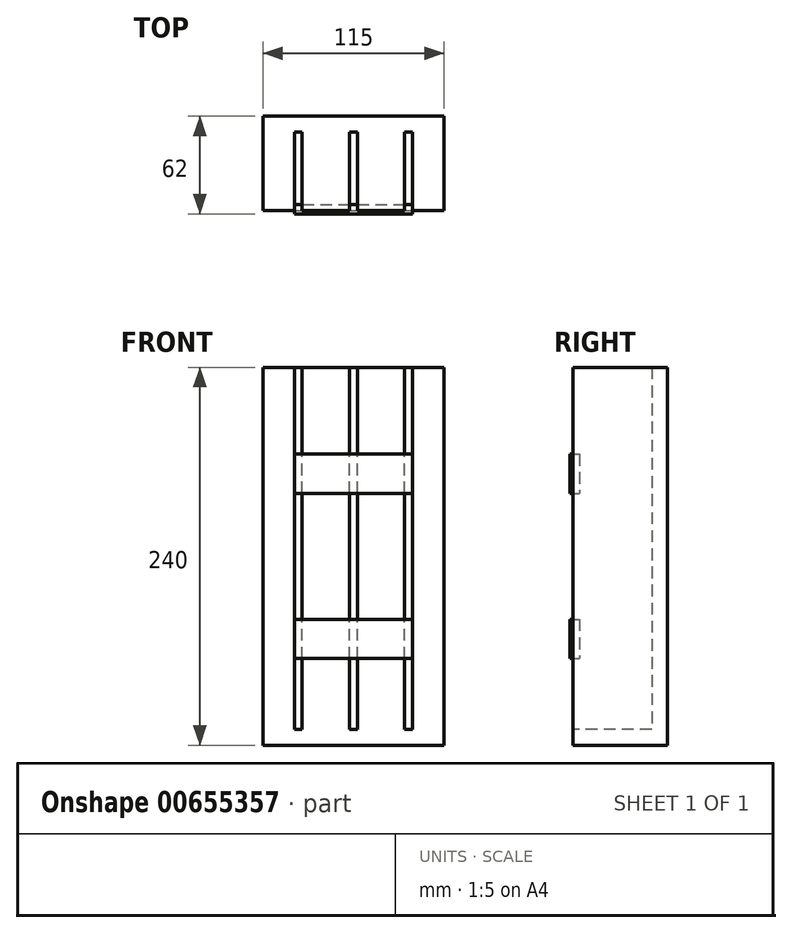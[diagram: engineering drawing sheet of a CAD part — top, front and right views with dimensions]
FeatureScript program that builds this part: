
annotation { "Feature Type Name" : "Feature", "Feature Type Description" : "" }
export const myFeature = defineFeature(function(context is Context, id is Id, definition is map)
    precondition{}
    {
        {
            var Q0;
            Q0=qCreatedBy(makeId("Front.planeOp"),FACE);
            var sketch = newSketch(context, id + "F0", { "sketchPlane" : qUnion([Q0])});
            skLineSegment(sketch, "E0.bottom", {"start": v(-57.5, 103.2) * mm, "end": v(57.5, 103.2) * mm});
            skLineSegment(sketch, "E0.top", {"start": v(-57.5, -136.8) * mm, "end": v(57.5, -136.8) * mm});
            skLineSegment(sketch, "E0.left", {"start": v(-57.5, 103.2) * mm, "end": v(-57.5, -136.8) * mm});
            skLineSegment(sketch, "E0.right", {"start": v(57.5, 103.2) * mm, "end": v(57.5, -136.8) * mm});
            skPoint(sketch, "E0.middle", {"position": v(0, -16.8) * mm});
            skLineSegment(sketch, "E1.bottom", {"start": v(-57.5, 103.2) * mm, "end": v(-37.5, 103.2) * mm});
            skLineSegment(sketch, "E1.top", {"start": v(-57.5, -136.8) * mm, "end": v(-37.5, -136.8) * mm});
            skLineSegment(sketch, "E1.right", {"start": v(-37.5, 103.2) * mm, "end": v(-37.5, -136.8) * mm});
            skLineSegment(sketch, "E2.bottom", {"start": v(57.5, 103.2) * mm, "end": v(37.5, 103.2) * mm});
            skLineSegment(sketch, "E2.top", {"start": v(57.5, -136.8) * mm, "end": v(37.5, -136.8) * mm});
            skLineSegment(sketch, "E2.right", {"start": v(37.5, 103.2) * mm, "end": v(37.5, -136.8) * mm});
            skLineSegment(sketch, "E3.bottom", {"start": v(-32.5, 103.2) * mm, "end": v(-2.5, 103.2) * mm});
            skLineSegment(sketch, "E3.top", {"start": v(-32.5, -126.8) * mm, "end": v(-2.5, -126.8) * mm});
            skLineSegment(sketch, "E3.left", {"start": v(-32.5, 103.2) * mm, "end": v(-32.5, -126.8) * mm});
            skLineSegment(sketch, "E3.right", {"start": v(-2.5, 103.2) * mm, "end": v(-2.5, -126.8) * mm});
            skLineSegment(sketch, "E4.bottom", {"start": v(2.5, 103.2) * mm, "end": v(32.5, 103.2) * mm});
            skLineSegment(sketch, "E4.top", {"start": v(2.5, -126.8) * mm, "end": v(32.5, -126.8) * mm});
            skLineSegment(sketch, "E4.left", {"start": v(2.5, 103.2) * mm, "end": v(2.5, -126.8) * mm});
            skLineSegment(sketch, "E4.right", {"start": v(32.5, 103.2) * mm, "end": v(32.5, -126.8) * mm});
            skLineSegment(sketch, "E5.top", {"start": v(-57.5, -126.8) * mm, "end": v(57.5, -126.8) * mm});
            skLineSegment(sketch, "E5.left", {"start": v(-57.5, -136.8) * mm, "end": v(-57.5, -126.8) * mm});
            skLineSegment(sketch, "E5.right", {"start": v(57.5, -136.8) * mm, "end": v(57.5, -126.8) * mm});
            skLineSegment(sketch, "E6.bottom", {"start": v(-57.5, 48.2) * mm, "end": v(57.5, 48.2) * mm});
            skLineSegment(sketch, "E6.top", {"start": v(-57.5, 23.2) * mm, "end": v(57.5, 23.2) * mm});
            skLineSegment(sketch, "E6.left", {"start": v(-57.5, 48.2) * mm, "end": v(-57.5, 23.2) * mm});
            skLineSegment(sketch, "E6.right", {"start": v(57.5, 48.2) * mm, "end": v(57.5, 23.2) * mm});
            skLineSegment(sketch, "E7.bottom", {"start": v(-57.5, -56.8) * mm, "end": v(57.5, -56.8) * mm});
            skLineSegment(sketch, "E7.top", {"start": v(-57.5, -81.8) * mm, "end": v(57.5, -81.8) * mm});
            skLineSegment(sketch, "E7.left", {"start": v(-57.5, -56.8) * mm, "end": v(-57.5, -81.8) * mm});
            skLineSegment(sketch, "E7.right", {"start": v(57.5, -56.8) * mm, "end": v(57.5, -81.8) * mm});
            skSolve(sketch);
        }
        {
            var Q0;
            Q0 = qSketchRegion(id + "F0", true);
            var Q1;
            {var subQ0=sQuery(id+"F0.wireOp",EDGE,"E7.top");var subQ1=sQuery(id+"F0.wireOp",EDGE,"E1.right");var subQ2=makeQuery(id+"F0.imprint","INTERSECT",VERTEX,{"derivedFrom":[subQ1,subQ0]});Q1=makeQuery(id+"F0.imprint","IMPRINT",FACE,{"disambiguationData":[TD([[makeQuery(id+"F0.imprint","IMPRINT",EDGE,{"disambiguationData":[TD([[subQ2,-1.0]])],"derivedFrom":subQ1}),1.0]])]});}
            var Q2;
            {var subQ0=sQuery(id+"F0.wireOp",EDGE,"E5.top");var subQ1=sQuery(id+"F0.wireOp",EDGE,"E3.left");var subQ2=makeQuery(id+"F0.imprint","INTERSECT",VERTEX,{"derivedFrom":[subQ1,subQ0]});Q2=makeQuery(id+"F0.imprint","IMPRINT",FACE,{"disambiguationData":[TD([[makeQuery(id+"F0.imprint","IMPRINT",EDGE,{"disambiguationData":[TD([[subQ2,1.0]])],"derivedFrom":subQ1}),1.0]])]});}
            var Q3;
            {var subQ0=sQuery(id+"F0.wireOp",EDGE,"E6.top");var subQ1=sQuery(id+"F0.wireOp",EDGE,"E3.left");var subQ2=makeQuery(id+"F0.imprint","INTERSECT",VERTEX,{"derivedFrom":[subQ1,subQ0]});Q3=makeQuery(id+"F0.imprint","IMPRINT",FACE,{"disambiguationData":[TD([[makeQuery(id+"F0.imprint","IMPRINT",EDGE,{"disambiguationData":[TD([[subQ2,-1.0]])],"derivedFrom":subQ1}),1.0]])]});}
            var Q4;
            {var subQ0=sQuery(id+"F0.wireOp",EDGE,"E6.bottom");var subQ1=sQuery(id+"F0.wireOp",EDGE,"E3.left");var subQ2=makeQuery(id+"F0.imprint","INTERSECT",VERTEX,{"derivedFrom":[subQ1,subQ0]});Q4=makeQuery(id+"F0.imprint","IMPRINT",FACE,{"disambiguationData":[TD([[makeQuery(id+"F0.imprint","IMPRINT",EDGE,{"disambiguationData":[TD([[subQ2,-1.0]])],"derivedFrom":subQ1}),1.0]])]});}
            var Q5;
            {var subQ0=sQuery(id+"F0.wireOp",EDGE,"E7.bottom");var subQ1=sQuery(id+"F0.wireOp",EDGE,"E3.left");var subQ2=makeQuery(id+"F0.imprint","INTERSECT",VERTEX,{"derivedFrom":[subQ1,subQ0]});Q5=makeQuery(id+"F0.imprint","IMPRINT",FACE,{"disambiguationData":[TD([[makeQuery(id+"F0.imprint","IMPRINT",EDGE,{"disambiguationData":[TD([[subQ2,-1.0]])],"derivedFrom":subQ1}),1.0]])]});}
            var Q6;
            {var subQ0=sQuery(id+"F0.wireOp",EDGE,"E7.bottom");var subQ1=sQuery(id+"F0.wireOp",EDGE,"E1.right");var subQ2=makeQuery(id+"F0.imprint","INTERSECT",VERTEX,{"derivedFrom":[subQ1,subQ0]});Q6=makeQuery(id+"F0.imprint","IMPRINT",FACE,{"disambiguationData":[TD([[makeQuery(id+"F0.imprint","IMPRINT",EDGE,{"disambiguationData":[TD([[subQ2,-1.0]])],"derivedFrom":subQ1}),1.0]])]});}
            var Q7;
            {var subQ0=sQuery(id+"F0.wireOp",EDGE,"E6.top");var subQ1=sQuery(id+"F0.wireOp",EDGE,"E1.right");var subQ2=makeQuery(id+"F0.imprint","INTERSECT",VERTEX,{"derivedFrom":[subQ1,subQ0]});Q7=makeQuery(id+"F0.imprint","IMPRINT",FACE,{"disambiguationData":[TD([[makeQuery(id+"F0.imprint","IMPRINT",EDGE,{"disambiguationData":[TD([[subQ2,-1.0]])],"derivedFrom":subQ1}),1.0]])]});}
            var Q8;
            {var subQ0=sQuery(id+"F0.wireOp",EDGE,"E6.bottom");var subQ1=sQuery(id+"F0.wireOp",EDGE,"E1.right");var subQ2=makeQuery(id+"F0.imprint","INTERSECT",VERTEX,{"derivedFrom":[subQ1,subQ0]});Q8=makeQuery(id+"F0.imprint","IMPRINT",FACE,{"disambiguationData":[TD([[makeQuery(id+"F0.imprint","IMPRINT",EDGE,{"disambiguationData":[TD([[subQ2,-1.0]])],"derivedFrom":subQ1}),1.0]])]});}
            var Q9;
            {var subQ0=sQuery(id+"F0.wireOp",EDGE,"E6.bottom");var subQ1=sQuery(id+"F0.wireOp",EDGE,"E3.right");var subQ2=makeQuery(id+"F0.imprint","INTERSECT",VERTEX,{"derivedFrom":[subQ1,subQ0]});Q9=makeQuery(id+"F0.imprint","IMPRINT",FACE,{"disambiguationData":[TD([[makeQuery(id+"F0.imprint","IMPRINT",EDGE,{"disambiguationData":[TD([[subQ2,-1.0]])],"derivedFrom":subQ1}),1.0]])]});}
            var Q10;
            {var subQ0=sQuery(id+"F0.wireOp",EDGE,"E6.bottom");var subQ1=sQuery(id+"F0.wireOp",EDGE,"E4.left");var subQ2=makeQuery(id+"F0.imprint","INTERSECT",VERTEX,{"derivedFrom":[subQ1,subQ0]});Q10=makeQuery(id+"F0.imprint","IMPRINT",FACE,{"disambiguationData":[TD([[makeQuery(id+"F0.imprint","IMPRINT",EDGE,{"disambiguationData":[TD([[subQ2,-1.0]])],"derivedFrom":subQ1}),1.0]])]});}
            var Q11;
            {var subQ0=sQuery(id+"F0.wireOp",EDGE,"E6.bottom");var subQ1=sQuery(id+"F0.wireOp",EDGE,"E2.right");var subQ2=makeQuery(id+"F0.imprint","INTERSECT",VERTEX,{"derivedFrom":[subQ1,subQ0]});Q11=makeQuery(id+"F0.imprint","IMPRINT",FACE,{"disambiguationData":[TD([[makeQuery(id+"F0.imprint","IMPRINT",EDGE,{"disambiguationData":[TD([[subQ2,-1.0]])],"derivedFrom":subQ1}),-1.0]])]});}
            var Q12;
            {var subQ0=sQuery(id+"F0.wireOp",EDGE,"E6.top");var subQ1=sQuery(id+"F0.wireOp",EDGE,"E2.right");var subQ2=makeQuery(id+"F0.imprint","INTERSECT",VERTEX,{"derivedFrom":[subQ1,subQ0]});Q12=makeQuery(id+"F0.imprint","IMPRINT",FACE,{"disambiguationData":[TD([[makeQuery(id+"F0.imprint","IMPRINT",EDGE,{"disambiguationData":[TD([[subQ2,-1.0]])],"derivedFrom":subQ1}),-1.0]])]});}
            var Q13;
            {var subQ0=sQuery(id+"F0.wireOp",EDGE,"E6.top");var subQ1=sQuery(id+"F0.wireOp",EDGE,"E4.left");var subQ2=makeQuery(id+"F0.imprint","INTERSECT",VERTEX,{"derivedFrom":[subQ1,subQ0]});Q13=makeQuery(id+"F0.imprint","IMPRINT",FACE,{"disambiguationData":[TD([[makeQuery(id+"F0.imprint","IMPRINT",EDGE,{"disambiguationData":[TD([[subQ2,-1.0]])],"derivedFrom":subQ1}),1.0]])]});}
            var Q14;
            {var subQ0=sQuery(id+"F0.wireOp",EDGE,"E6.top");var subQ1=sQuery(id+"F0.wireOp",EDGE,"E3.right");var subQ2=makeQuery(id+"F0.imprint","INTERSECT",VERTEX,{"derivedFrom":[subQ1,subQ0]});Q14=makeQuery(id+"F0.imprint","IMPRINT",FACE,{"disambiguationData":[TD([[makeQuery(id+"F0.imprint","IMPRINT",EDGE,{"disambiguationData":[TD([[subQ2,-1.0]])],"derivedFrom":subQ1}),1.0]])]});}
            var Q15;
            {var subQ0=sQuery(id+"F0.wireOp",EDGE,"E6.top");var subQ1=sQuery(id+"F0.wireOp",EDGE,"E3.right");var subQ2=makeQuery(id+"F0.imprint","INTERSECT",VERTEX,{"derivedFrom":[subQ1,subQ0]});Q15=makeQuery(id+"F0.imprint","IMPRINT",FACE,{"disambiguationData":[TD([[makeQuery(id+"F0.imprint","IMPRINT",EDGE,{"disambiguationData":[TD([[subQ2,-1.0]])],"derivedFrom":subQ1}),1.0]])]});}
            var Q16;
            {var subQ0=sQuery(id+"F0.wireOp",EDGE,"E6.top");var subQ1=sQuery(id+"F0.wireOp",EDGE,"E4.left");var subQ2=makeQuery(id+"F0.imprint","INTERSECT",VERTEX,{"derivedFrom":[subQ1,subQ0]});Q16=makeQuery(id+"F0.imprint","IMPRINT",FACE,{"disambiguationData":[TD([[makeQuery(id+"F0.imprint","IMPRINT",EDGE,{"disambiguationData":[TD([[subQ2,-1.0]])],"derivedFrom":subQ1}),1.0]])]});}
            var Q17;
            {var subQ0=sQuery(id+"F0.wireOp",EDGE,"E7.bottom");var subQ1=sQuery(id+"F0.wireOp",EDGE,"E3.right");var subQ2=makeQuery(id+"F0.imprint","INTERSECT",VERTEX,{"derivedFrom":[subQ1,subQ0]});Q17=makeQuery(id+"F0.imprint","IMPRINT",FACE,{"disambiguationData":[TD([[makeQuery(id+"F0.imprint","IMPRINT",EDGE,{"disambiguationData":[TD([[subQ2,-1.0]])],"derivedFrom":subQ1}),1.0]])]});}
            var Q18;
            {var subQ0=sQuery(id+"F0.wireOp",EDGE,"E5.top");var subQ1=sQuery(id+"F0.wireOp",EDGE,"E3.right");var subQ2=makeQuery(id+"F0.imprint","INTERSECT",VERTEX,{"derivedFrom":[subQ1,subQ0]});Q18=makeQuery(id+"F0.imprint","IMPRINT",FACE,{"disambiguationData":[TD([[makeQuery(id+"F0.imprint","IMPRINT",EDGE,{"disambiguationData":[TD([[subQ2,1.0]])],"derivedFrom":subQ1}),1.0]])]});}
            var Q19;
            {var subQ0=sQuery(id+"F0.wireOp",EDGE,"E5.top");var subQ1=sQuery(id+"F0.wireOp",EDGE,"E4.left");var subQ2=makeQuery(id+"F0.imprint","INTERSECT",VERTEX,{"derivedFrom":[subQ1,subQ0]});Q19=makeQuery(id+"F0.imprint","IMPRINT",FACE,{"disambiguationData":[TD([[makeQuery(id+"F0.imprint","IMPRINT",EDGE,{"disambiguationData":[TD([[subQ2,1.0]])],"derivedFrom":subQ1}),1.0]])]});}
            var Q20;
            {var subQ0=sQuery(id+"F0.wireOp",EDGE,"E7.top");var subQ1=sQuery(id+"F0.wireOp",EDGE,"E2.right");var subQ2=makeQuery(id+"F0.imprint","INTERSECT",VERTEX,{"derivedFrom":[subQ1,subQ0]});Q20=makeQuery(id+"F0.imprint","IMPRINT",FACE,{"disambiguationData":[TD([[makeQuery(id+"F0.imprint","IMPRINT",EDGE,{"disambiguationData":[TD([[subQ2,-1.0]])],"derivedFrom":subQ1}),-1.0]])]});}
            var Q21;
            {var subQ0=sQuery(id+"F0.wireOp",EDGE,"E7.bottom");var subQ1=sQuery(id+"F0.wireOp",EDGE,"E2.right");var subQ2=makeQuery(id+"F0.imprint","INTERSECT",VERTEX,{"derivedFrom":[subQ1,subQ0]});Q21=makeQuery(id+"F0.imprint","IMPRINT",FACE,{"disambiguationData":[TD([[makeQuery(id+"F0.imprint","IMPRINT",EDGE,{"disambiguationData":[TD([[subQ2,-1.0]])],"derivedFrom":subQ1}),-1.0]])]});}
            var Q22;
            {var subQ0=sQuery(id+"F0.wireOp",EDGE,"E7.bottom");var subQ1=sQuery(id+"F0.wireOp",EDGE,"E4.left");var subQ2=makeQuery(id+"F0.imprint","INTERSECT",VERTEX,{"derivedFrom":[subQ1,subQ0]});Q22=makeQuery(id+"F0.imprint","IMPRINT",FACE,{"disambiguationData":[TD([[makeQuery(id+"F0.imprint","IMPRINT",EDGE,{"disambiguationData":[TD([[subQ2,-1.0]])],"derivedFrom":subQ1}),1.0]])]});}
            extrude(context, id + "F1", {"entities" : qUnion([Q0, Q1, Q2, Q3, Q4, Q5, Q6, Q7, Q8, Q9, Q10, Q11, Q12, Q13, Q14, Q15, Q16, Q17, Q18, Q19, Q20, Q21, Q22]), "oppositeDirection" : true, "depth" : 60 * mm, "offsetDistance" : 25 * mm});
        }
        {
            var Q0;
            {var subQ0=sQuery(id+"F0.wireOp",EDGE,"E1.right");var subQ5=sQuery(id+"F0.wireOp",EDGE,"E6.bottom");var subQ6=makeQuery(id+"F0.imprint","INTERSECT",VERTEX,{"derivedFrom":[subQ0,subQ5]});Q0=makeQuery(id+"F0.imprint","IMPRINT",FACE,{"disambiguationData":[TD([[makeQuery(id+"F0.imprint","IMPRINT",EDGE,{"disambiguationData":[TD([[subQ6,-1.0]])],"derivedFrom":subQ5}),1.0]])]});}
            var Q1;
            {var subQ0=sQuery(id+"F0.wireOp",EDGE,"E6.bottom");var subQ1=sQuery(id+"F0.wireOp",EDGE,"E1.right");var subQ2=makeQuery(id+"F0.imprint","INTERSECT",VERTEX,{"derivedFrom":[subQ1,subQ0]});Q1=makeQuery(id+"F0.imprint","IMPRINT",FACE,{"disambiguationData":[TD([[makeQuery(id+"F0.imprint","IMPRINT",EDGE,{"disambiguationData":[TD([[subQ2,-1.0]])],"derivedFrom":subQ1}),1.0]])]});}
            var Q2;
            {var subQ0=sQuery(id+"F0.wireOp",EDGE,"E6.top");var subQ1=sQuery(id+"F0.wireOp",EDGE,"E1.right");var subQ2=makeQuery(id+"F0.imprint","INTERSECT",VERTEX,{"derivedFrom":[subQ1,subQ0]});Q2=makeQuery(id+"F0.imprint","IMPRINT",FACE,{"disambiguationData":[TD([[makeQuery(id+"F0.imprint","IMPRINT",EDGE,{"disambiguationData":[TD([[subQ2,-1.0]])],"derivedFrom":subQ1}),1.0]])]});}
            var Q3;
            {var subQ0=sQuery(id+"F0.wireOp",EDGE,"E7.bottom");var subQ1=sQuery(id+"F0.wireOp",EDGE,"E1.right");var subQ2=makeQuery(id+"F0.imprint","INTERSECT",VERTEX,{"derivedFrom":[subQ1,subQ0]});Q3=makeQuery(id+"F0.imprint","IMPRINT",FACE,{"disambiguationData":[TD([[makeQuery(id+"F0.imprint","IMPRINT",EDGE,{"disambiguationData":[TD([[subQ2,-1.0]])],"derivedFrom":subQ1}),1.0]])]});}
            var Q4;
            {var subQ0=sQuery(id+"F0.wireOp",EDGE,"E7.top");var subQ1=sQuery(id+"F0.wireOp",EDGE,"E1.right");var subQ2=makeQuery(id+"F0.imprint","INTERSECT",VERTEX,{"derivedFrom":[subQ1,subQ0]});Q4=makeQuery(id+"F0.imprint","IMPRINT",FACE,{"disambiguationData":[TD([[makeQuery(id+"F0.imprint","IMPRINT",EDGE,{"disambiguationData":[TD([[subQ2,-1.0]])],"derivedFrom":subQ1}),1.0]])]});}
            var Q5;
            {var subQ0=sQuery(id+"F0.wireOp",EDGE,"E5.top");var subQ1=sQuery(id+"F0.wireOp",EDGE,"E3.right");var subQ2=makeQuery(id+"F0.imprint","INTERSECT",VERTEX,{"derivedFrom":[subQ1,subQ0]});Q5=makeQuery(id+"F0.imprint","IMPRINT",FACE,{"disambiguationData":[TD([[makeQuery(id+"F0.imprint","IMPRINT",EDGE,{"disambiguationData":[TD([[subQ2,1.0]])],"derivedFrom":subQ1}),1.0]])]});}
            var Q6;
            {var subQ0=sQuery(id+"F0.wireOp",EDGE,"E7.bottom");var subQ1=sQuery(id+"F0.wireOp",EDGE,"E3.right");var subQ2=makeQuery(id+"F0.imprint","INTERSECT",VERTEX,{"derivedFrom":[subQ1,subQ0]});Q6=makeQuery(id+"F0.imprint","IMPRINT",FACE,{"disambiguationData":[TD([[makeQuery(id+"F0.imprint","IMPRINT",EDGE,{"disambiguationData":[TD([[subQ2,-1.0]])],"derivedFrom":subQ1}),1.0]])]});}
            var Q7;
            {var subQ0=sQuery(id+"F0.wireOp",EDGE,"E6.top");var subQ1=sQuery(id+"F0.wireOp",EDGE,"E3.right");var subQ2=makeQuery(id+"F0.imprint","INTERSECT",VERTEX,{"derivedFrom":[subQ1,subQ0]});Q7=makeQuery(id+"F0.imprint","IMPRINT",FACE,{"disambiguationData":[TD([[makeQuery(id+"F0.imprint","IMPRINT",EDGE,{"disambiguationData":[TD([[subQ2,-1.0]])],"derivedFrom":subQ1}),1.0]])]});}
            var Q8;
            {var subQ0=sQuery(id+"F0.wireOp",EDGE,"E6.bottom");var subQ1=sQuery(id+"F0.wireOp",EDGE,"E3.right");var subQ2=makeQuery(id+"F0.imprint","INTERSECT",VERTEX,{"derivedFrom":[subQ1,subQ0]});Q8=makeQuery(id+"F0.imprint","IMPRINT",FACE,{"disambiguationData":[TD([[makeQuery(id+"F0.imprint","IMPRINT",EDGE,{"disambiguationData":[TD([[subQ2,-1.0]])],"derivedFrom":subQ1}),1.0]])]});}
            var Q9;
            {var subQ0=sQuery(id+"F0.wireOp",EDGE,"E3.right");var subQ5=sQuery(id+"F0.wireOp",EDGE,"E6.bottom");var subQ6=makeQuery(id+"F0.imprint","INTERSECT",VERTEX,{"derivedFrom":[subQ0,subQ5]});Q9=makeQuery(id+"F0.imprint","IMPRINT",FACE,{"disambiguationData":[TD([[makeQuery(id+"F0.imprint","IMPRINT",EDGE,{"disambiguationData":[TD([[subQ6,-1.0]])],"derivedFrom":subQ5}),1.0]])]});}
            var Q10;
            {var subQ0=sQuery(id+"F0.wireOp",EDGE,"E2.right");var subQ5=sQuery(id+"F0.wireOp",EDGE,"E6.bottom");var subQ6=makeQuery(id+"F0.imprint","INTERSECT",VERTEX,{"derivedFrom":[subQ0,subQ5]});Q10=makeQuery(id+"F0.imprint","IMPRINT",FACE,{"disambiguationData":[TD([[makeQuery(id+"F0.imprint","IMPRINT",EDGE,{"disambiguationData":[TD([[subQ6,1.0]])],"derivedFrom":subQ5}),1.0]])]});}
            var Q11;
            {var subQ0=sQuery(id+"F0.wireOp",EDGE,"E6.bottom");var subQ1=sQuery(id+"F0.wireOp",EDGE,"E2.right");var subQ2=makeQuery(id+"F0.imprint","INTERSECT",VERTEX,{"derivedFrom":[subQ1,subQ0]});Q11=makeQuery(id+"F0.imprint","IMPRINT",FACE,{"disambiguationData":[TD([[makeQuery(id+"F0.imprint","IMPRINT",EDGE,{"disambiguationData":[TD([[subQ2,-1.0]])],"derivedFrom":subQ1}),-1.0]])]});}
            var Q12;
            {var subQ0=sQuery(id+"F0.wireOp",EDGE,"E6.top");var subQ1=sQuery(id+"F0.wireOp",EDGE,"E2.right");var subQ2=makeQuery(id+"F0.imprint","INTERSECT",VERTEX,{"derivedFrom":[subQ1,subQ0]});Q12=makeQuery(id+"F0.imprint","IMPRINT",FACE,{"disambiguationData":[TD([[makeQuery(id+"F0.imprint","IMPRINT",EDGE,{"disambiguationData":[TD([[subQ2,-1.0]])],"derivedFrom":subQ1}),-1.0]])]});}
            var Q13;
            {var subQ0=sQuery(id+"F0.wireOp",EDGE,"E7.top");var subQ1=sQuery(id+"F0.wireOp",EDGE,"E2.right");var subQ2=makeQuery(id+"F0.imprint","INTERSECT",VERTEX,{"derivedFrom":[subQ1,subQ0]});Q13=makeQuery(id+"F0.imprint","IMPRINT",FACE,{"disambiguationData":[TD([[makeQuery(id+"F0.imprint","IMPRINT",EDGE,{"disambiguationData":[TD([[subQ2,-1.0]])],"derivedFrom":subQ1}),-1.0]])]});}
            var Q14;
            {var subQ0=sQuery(id+"F0.wireOp",EDGE,"E7.bottom");var subQ1=sQuery(id+"F0.wireOp",EDGE,"E2.right");var subQ2=makeQuery(id+"F0.imprint","INTERSECT",VERTEX,{"derivedFrom":[subQ1,subQ0]});Q14=makeQuery(id+"F0.imprint","IMPRINT",FACE,{"disambiguationData":[TD([[makeQuery(id+"F0.imprint","IMPRINT",EDGE,{"disambiguationData":[TD([[subQ2,-1.0]])],"derivedFrom":subQ1}),-1.0]])]});}
            extrude(context, id + "F2", {"entities" : qUnion([Q0, Q1, Q2, Q3, Q4, Q5, Q6, Q7, Q8, Q9, Q10, Q11, Q12, Q13, Q14]), "operationType" : NewBodyOperationType.REMOVE, "oppositeDirection" : true, "depth" : 50 * mm, "offsetDistance" : 25 * mm});
        }
        {
            var Q0;
            {var subQ5=sQuery(id+"F0.wireOp",EDGE,"E6.left");Q0=makeQuery(id+"F0.imprint","IMPRINT",FACE,{"disambiguationData":[TD([[makeQuery(id+"F0.imprint","IMPRINT",EDGE,{"derivedFrom":subQ5}),1.0]])]});}
            var Q1;
            {var subQ0=sQuery(id+"F0.wireOp",EDGE,"E6.bottom");var subQ1=sQuery(id+"F0.wireOp",EDGE,"E1.right");var subQ2=makeQuery(id+"F0.imprint","INTERSECT",VERTEX,{"derivedFrom":[subQ1,subQ0]});Q1=makeQuery(id+"F0.imprint","IMPRINT",FACE,{"disambiguationData":[TD([[makeQuery(id+"F0.imprint","IMPRINT",EDGE,{"disambiguationData":[TD([[subQ2,-1.0]])],"derivedFrom":subQ1}),1.0]])]});}
            var Q2;
            {var subQ0=sQuery(id+"F0.wireOp",EDGE,"E6.bottom");var subQ1=sQuery(id+"F0.wireOp",EDGE,"E3.left");var subQ2=makeQuery(id+"F0.imprint","INTERSECT",VERTEX,{"derivedFrom":[subQ1,subQ0]});Q2=makeQuery(id+"F0.imprint","IMPRINT",FACE,{"disambiguationData":[TD([[makeQuery(id+"F0.imprint","IMPRINT",EDGE,{"disambiguationData":[TD([[subQ2,-1.0]])],"derivedFrom":subQ1}),1.0]])]});}
            var Q3;
            {var subQ0=sQuery(id+"F0.wireOp",EDGE,"E6.bottom");var subQ1=sQuery(id+"F0.wireOp",EDGE,"E3.right");var subQ2=makeQuery(id+"F0.imprint","INTERSECT",VERTEX,{"derivedFrom":[subQ1,subQ0]});Q3=makeQuery(id+"F0.imprint","IMPRINT",FACE,{"disambiguationData":[TD([[makeQuery(id+"F0.imprint","IMPRINT",EDGE,{"disambiguationData":[TD([[subQ2,-1.0]])],"derivedFrom":subQ1}),1.0]])]});}
            var Q4;
            {var subQ0=sQuery(id+"F0.wireOp",EDGE,"E6.bottom");var subQ1=sQuery(id+"F0.wireOp",EDGE,"E4.left");var subQ2=makeQuery(id+"F0.imprint","INTERSECT",VERTEX,{"derivedFrom":[subQ1,subQ0]});Q4=makeQuery(id+"F0.imprint","IMPRINT",FACE,{"disambiguationData":[TD([[makeQuery(id+"F0.imprint","IMPRINT",EDGE,{"disambiguationData":[TD([[subQ2,-1.0]])],"derivedFrom":subQ1}),1.0]])]});}
            var Q5;
            {var subQ0=sQuery(id+"F0.wireOp",EDGE,"E6.bottom");var subQ1=sQuery(id+"F0.wireOp",EDGE,"E2.right");var subQ2=makeQuery(id+"F0.imprint","INTERSECT",VERTEX,{"derivedFrom":[subQ1,subQ0]});Q5=makeQuery(id+"F0.imprint","IMPRINT",FACE,{"disambiguationData":[TD([[makeQuery(id+"F0.imprint","IMPRINT",EDGE,{"disambiguationData":[TD([[subQ2,-1.0]])],"derivedFrom":subQ1}),-1.0]])]});}
            var Q6;
            {var subQ5=sQuery(id+"F0.wireOp",EDGE,"E6.right");Q6=makeQuery(id+"F0.imprint","IMPRINT",FACE,{"disambiguationData":[TD([[makeQuery(id+"F0.imprint","IMPRINT",EDGE,{"derivedFrom":subQ5}),-1.0]])]});}
            var Q7;
            {var subQ5=sQuery(id+"F0.wireOp",EDGE,"E7.left");Q7=makeQuery(id+"F0.imprint","IMPRINT",FACE,{"disambiguationData":[TD([[makeQuery(id+"F0.imprint","IMPRINT",EDGE,{"derivedFrom":subQ5}),1.0]])]});}
            var Q8;
            {var subQ0=sQuery(id+"F0.wireOp",EDGE,"E7.bottom");var subQ1=sQuery(id+"F0.wireOp",EDGE,"E1.right");var subQ2=makeQuery(id+"F0.imprint","INTERSECT",VERTEX,{"derivedFrom":[subQ1,subQ0]});Q8=makeQuery(id+"F0.imprint","IMPRINT",FACE,{"disambiguationData":[TD([[makeQuery(id+"F0.imprint","IMPRINT",EDGE,{"disambiguationData":[TD([[subQ2,-1.0]])],"derivedFrom":subQ1}),1.0]])]});}
            var Q9;
            {var subQ0=sQuery(id+"F0.wireOp",EDGE,"E7.bottom");var subQ1=sQuery(id+"F0.wireOp",EDGE,"E3.left");var subQ2=makeQuery(id+"F0.imprint","INTERSECT",VERTEX,{"derivedFrom":[subQ1,subQ0]});Q9=makeQuery(id+"F0.imprint","IMPRINT",FACE,{"disambiguationData":[TD([[makeQuery(id+"F0.imprint","IMPRINT",EDGE,{"disambiguationData":[TD([[subQ2,-1.0]])],"derivedFrom":subQ1}),1.0]])]});}
            var Q10;
            {var subQ0=sQuery(id+"F0.wireOp",EDGE,"E7.bottom");var subQ1=sQuery(id+"F0.wireOp",EDGE,"E3.right");var subQ2=makeQuery(id+"F0.imprint","INTERSECT",VERTEX,{"derivedFrom":[subQ1,subQ0]});Q10=makeQuery(id+"F0.imprint","IMPRINT",FACE,{"disambiguationData":[TD([[makeQuery(id+"F0.imprint","IMPRINT",EDGE,{"disambiguationData":[TD([[subQ2,-1.0]])],"derivedFrom":subQ1}),1.0]])]});}
            var Q11;
            {var subQ0=sQuery(id+"F0.wireOp",EDGE,"E7.bottom");var subQ1=sQuery(id+"F0.wireOp",EDGE,"E2.right");var subQ2=makeQuery(id+"F0.imprint","INTERSECT",VERTEX,{"derivedFrom":[subQ1,subQ0]});Q11=makeQuery(id+"F0.imprint","IMPRINT",FACE,{"disambiguationData":[TD([[makeQuery(id+"F0.imprint","IMPRINT",EDGE,{"disambiguationData":[TD([[subQ2,-1.0]])],"derivedFrom":subQ1}),-1.0]])]});}
            var Q12;
            {var subQ5=sQuery(id+"F0.wireOp",EDGE,"E7.right");Q12=makeQuery(id+"F0.imprint","IMPRINT",FACE,{"disambiguationData":[TD([[makeQuery(id+"F0.imprint","IMPRINT",EDGE,{"derivedFrom":subQ5}),-1.0]])]});}
            var Q13;
            {var subQ0=sQuery(id+"F0.wireOp",EDGE,"E7.bottom");var subQ1=sQuery(id+"F0.wireOp",EDGE,"E4.left");var subQ2=makeQuery(id+"F0.imprint","INTERSECT",VERTEX,{"derivedFrom":[subQ1,subQ0]});Q13=makeQuery(id+"F0.imprint","IMPRINT",FACE,{"disambiguationData":[TD([[makeQuery(id+"F0.imprint","IMPRINT",EDGE,{"disambiguationData":[TD([[subQ2,-1.0]])],"derivedFrom":subQ1}),1.0]])]});}
            extrude(context, id + "F3", {"entities" : qUnion([Q0, Q1, Q2, Q3, Q4, Q5, Q6, Q7, Q8, Q9, Q10, Q11, Q12, Q13]), "operationType" : NewBodyOperationType.REMOVE, "oppositeDirection" : true, "depth" : 4 * mm, "offsetDistance" : 25 * mm});
        }
        {
            var Q0;
            {var subQ5=sQuery(id+"F0.wireOp",EDGE,"E6.left");Q0=makeQuery(id+"F0.imprint","IMPRINT",FACE,{"disambiguationData":[TD([[makeQuery(id+"F0.imprint","IMPRINT",EDGE,{"derivedFrom":subQ5}),1.0]])]});}
            var Q1;
            {var subQ0=sQuery(id+"F0.wireOp",EDGE,"E6.bottom");var subQ1=sQuery(id+"F0.wireOp",EDGE,"E1.right");var subQ2=makeQuery(id+"F0.imprint","INTERSECT",VERTEX,{"derivedFrom":[subQ1,subQ0]});Q1=makeQuery(id+"F0.imprint","IMPRINT",FACE,{"disambiguationData":[TD([[makeQuery(id+"F0.imprint","IMPRINT",EDGE,{"disambiguationData":[TD([[subQ2,-1.0]])],"derivedFrom":subQ1}),1.0]])]});}
            var Q2;
            {var subQ0=sQuery(id+"F0.wireOp",EDGE,"E6.bottom");var subQ1=sQuery(id+"F0.wireOp",EDGE,"E3.right");var subQ2=makeQuery(id+"F0.imprint","INTERSECT",VERTEX,{"derivedFrom":[subQ1,subQ0]});Q2=makeQuery(id+"F0.imprint","IMPRINT",FACE,{"disambiguationData":[TD([[makeQuery(id+"F0.imprint","IMPRINT",EDGE,{"disambiguationData":[TD([[subQ2,-1.0]])],"derivedFrom":subQ1}),1.0]])]});}
            var Q3;
            {var subQ0=sQuery(id+"F0.wireOp",EDGE,"E6.bottom");var subQ1=sQuery(id+"F0.wireOp",EDGE,"E4.left");var subQ2=makeQuery(id+"F0.imprint","INTERSECT",VERTEX,{"derivedFrom":[subQ1,subQ0]});Q3=makeQuery(id+"F0.imprint","IMPRINT",FACE,{"disambiguationData":[TD([[makeQuery(id+"F0.imprint","IMPRINT",EDGE,{"disambiguationData":[TD([[subQ2,-1.0]])],"derivedFrom":subQ1}),1.0]])]});}
            var Q4;
            {var subQ5=sQuery(id+"F0.wireOp",EDGE,"E6.right");Q4=makeQuery(id+"F0.imprint","IMPRINT",FACE,{"disambiguationData":[TD([[makeQuery(id+"F0.imprint","IMPRINT",EDGE,{"derivedFrom":subQ5}),-1.0]])]});}
            var Q5;
            {var subQ0=sQuery(id+"F0.wireOp",EDGE,"E6.bottom");var subQ1=sQuery(id+"F0.wireOp",EDGE,"E3.left");var subQ2=makeQuery(id+"F0.imprint","INTERSECT",VERTEX,{"derivedFrom":[subQ1,subQ0]});Q5=makeQuery(id+"F0.imprint","IMPRINT",FACE,{"disambiguationData":[TD([[makeQuery(id+"F0.imprint","IMPRINT",EDGE,{"disambiguationData":[TD([[subQ2,-1.0]])],"derivedFrom":subQ1}),1.0]])]});}
            var Q6;
            {var subQ0=sQuery(id+"F0.wireOp",EDGE,"E6.bottom");var subQ1=sQuery(id+"F0.wireOp",EDGE,"E2.right");var subQ2=makeQuery(id+"F0.imprint","INTERSECT",VERTEX,{"derivedFrom":[subQ1,subQ0]});Q6=makeQuery(id+"F0.imprint","IMPRINT",FACE,{"disambiguationData":[TD([[makeQuery(id+"F0.imprint","IMPRINT",EDGE,{"disambiguationData":[TD([[subQ2,-1.0]])],"derivedFrom":subQ1}),-1.0]])]});}
            extrude(context, id + "F4", {"entities" : qUnion([Q0, Q1, Q2, Q3, Q4, Q5, Q6]), "depth" : 2 * mm, "offsetDistance" : 25 * mm, "hasSecondDirection" : true, "secondDirectionOppositeDirection" : true, "secondDirectionDepth" : 4 * mm});
        }
        {
            var Q0;
            {var subQ5=sQuery(id+"F0.wireOp",EDGE,"E7.left");Q0=makeQuery(id+"F0.imprint","IMPRINT",FACE,{"disambiguationData":[TD([[makeQuery(id+"F0.imprint","IMPRINT",EDGE,{"derivedFrom":subQ5}),1.0]])]});}
            var Q1;
            {var subQ0=sQuery(id+"F0.wireOp",EDGE,"E7.bottom");var subQ1=sQuery(id+"F0.wireOp",EDGE,"E1.right");var subQ2=makeQuery(id+"F0.imprint","INTERSECT",VERTEX,{"derivedFrom":[subQ1,subQ0]});Q1=makeQuery(id+"F0.imprint","IMPRINT",FACE,{"disambiguationData":[TD([[makeQuery(id+"F0.imprint","IMPRINT",EDGE,{"disambiguationData":[TD([[subQ2,-1.0]])],"derivedFrom":subQ1}),1.0]])]});}
            var Q2;
            {var subQ0=sQuery(id+"F0.wireOp",EDGE,"E7.bottom");var subQ1=sQuery(id+"F0.wireOp",EDGE,"E3.left");var subQ2=makeQuery(id+"F0.imprint","INTERSECT",VERTEX,{"derivedFrom":[subQ1,subQ0]});Q2=makeQuery(id+"F0.imprint","IMPRINT",FACE,{"disambiguationData":[TD([[makeQuery(id+"F0.imprint","IMPRINT",EDGE,{"disambiguationData":[TD([[subQ2,-1.0]])],"derivedFrom":subQ1}),1.0]])]});}
            var Q3;
            {var subQ0=sQuery(id+"F0.wireOp",EDGE,"E7.bottom");var subQ1=sQuery(id+"F0.wireOp",EDGE,"E3.right");var subQ2=makeQuery(id+"F0.imprint","INTERSECT",VERTEX,{"derivedFrom":[subQ1,subQ0]});Q3=makeQuery(id+"F0.imprint","IMPRINT",FACE,{"disambiguationData":[TD([[makeQuery(id+"F0.imprint","IMPRINT",EDGE,{"disambiguationData":[TD([[subQ2,-1.0]])],"derivedFrom":subQ1}),1.0]])]});}
            var Q4;
            {var subQ0=sQuery(id+"F0.wireOp",EDGE,"E7.bottom");var subQ1=sQuery(id+"F0.wireOp",EDGE,"E4.left");var subQ2=makeQuery(id+"F0.imprint","INTERSECT",VERTEX,{"derivedFrom":[subQ1,subQ0]});Q4=makeQuery(id+"F0.imprint","IMPRINT",FACE,{"disambiguationData":[TD([[makeQuery(id+"F0.imprint","IMPRINT",EDGE,{"disambiguationData":[TD([[subQ2,-1.0]])],"derivedFrom":subQ1}),1.0]])]});}
            var Q5;
            {var subQ0=sQuery(id+"F0.wireOp",EDGE,"E7.bottom");var subQ1=sQuery(id+"F0.wireOp",EDGE,"E2.right");var subQ2=makeQuery(id+"F0.imprint","INTERSECT",VERTEX,{"derivedFrom":[subQ1,subQ0]});Q5=makeQuery(id+"F0.imprint","IMPRINT",FACE,{"disambiguationData":[TD([[makeQuery(id+"F0.imprint","IMPRINT",EDGE,{"disambiguationData":[TD([[subQ2,-1.0]])],"derivedFrom":subQ1}),-1.0]])]});}
            var Q6;
            {var subQ5=sQuery(id+"F0.wireOp",EDGE,"E7.right");Q6=makeQuery(id+"F0.imprint","IMPRINT",FACE,{"disambiguationData":[TD([[makeQuery(id+"F0.imprint","IMPRINT",EDGE,{"derivedFrom":subQ5}),-1.0]])]});}
            extrude(context, id + "F5", {"entities" : qUnion([Q0, Q1, Q2, Q3, Q4, Q5, Q6]), "depth" : 2 * mm, "offsetDistance" : 25 * mm, "hasSecondDirection" : true, "secondDirectionOppositeDirection" : true, "secondDirectionDepth" : 4 * mm});
        }
    });
